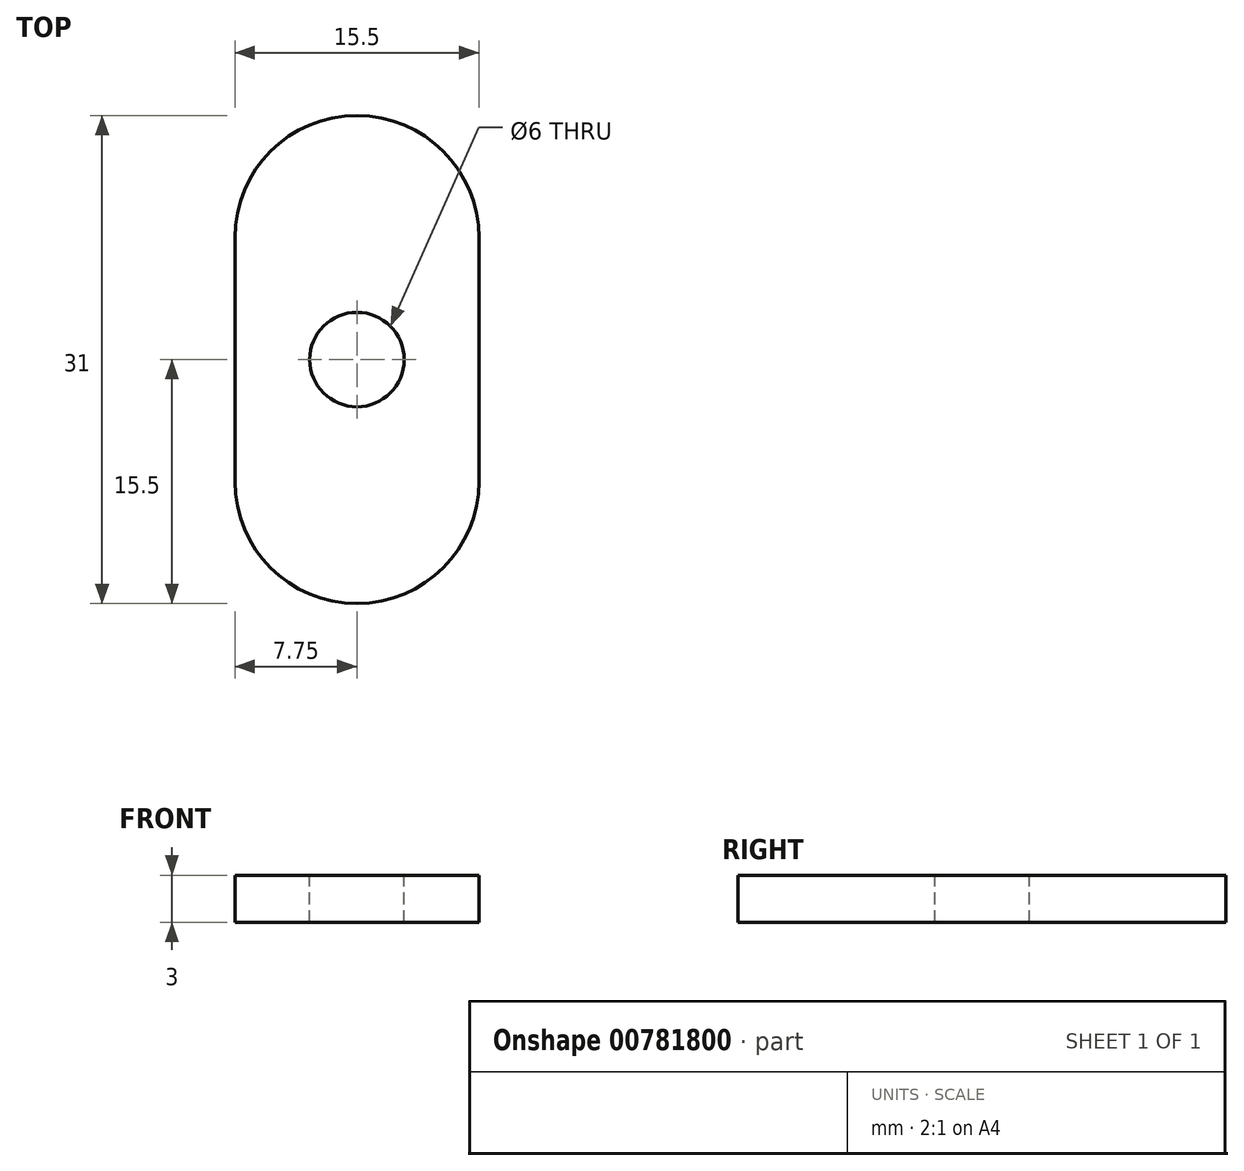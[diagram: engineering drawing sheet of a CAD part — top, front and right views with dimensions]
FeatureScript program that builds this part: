
annotation { "Feature Type Name" : "Feature", "Feature Type Description" : "" }
export const myFeature = defineFeature(function(context is Context, id is Id, definition is map)
    precondition{}
    {
        {
            var Q0;
            Q0=qCreatedBy(makeId("Top.planeOp"),FACE);
            var sketch = newSketch(context, id + "F0", { "sketchPlane" : qUnion([Q0])});
            skPoint(sketch, "E0.middle", {"position": v(0, 0) * mm});
            skPoint(sketch, "E0.top.end.orphan", {"position": v(7.75, -7.75) * mm});
            skPoint(sketch, "E0.left.end.orphan", {"position": v(-5.42, -5.42) * mm});
            skPoint(sketch, "E1.start.orphan", {"position": v(-7.75, 7.75) * mm});
            skPoint(sketch, "E0.bottom.end.orphan", {"position": v(5.42, 5.42) * mm});
            skLineSegment(sketch, "E2.left", {"start": v(-7.75, 7.75) * mm, "end": v(-7.75, -7.75) * mm});
            skLineSegment(sketch, "E2.right", {"start": v(7.75, 7.75) * mm, "end": v(7.75, -7.75) * mm});
            skArc(sketch, "E3", {"start": v(-7.75, 7.75) * mm, "mid": v(0, 15.5) * mm, "end": v(7.75, 7.75) * mm});
            skArc(sketch, "E4", {"start": v(-7.75, -7.75) * mm, "mid": v(0, -15.5) * mm, "end": v(7.75, -7.75) * mm});
            skSolve(sketch);
        }
        {
            var Q0;
            Q0 = qSketchRegion(id + "F0", true);
            extrude(context, id + "F1", {"entities" : qUnion([Q0]), "depth" : 3 * mm, "offsetDistance" : 25 * mm});
        }
        {
            var Q0;
            Q0=makeQuery(id+"F1.opExtrude","CAP_FACE",FACE,{"disambiguationData":[OSD([sQuery(id+"F0.wireOp",EDGE,"E2.left"),sQuery(id+"F0.wireOp",EDGE,"E2.right"),sQuery(id+"F0.wireOp",EDGE,"E3"),sQuery(id+"F0.wireOp",EDGE,"E4")])],"isStart":false});
            var sketch = newSketch(context, id + "F2", { "sketchPlane" : qUnion([Q0])});
            skCircle(sketch, "E5", {"center": v(0, 0) * mm, "radius": 3 * mm});
            skSolve(sketch);
        }
        {
            var Q0;
            Q0 = qSketchRegion(id + "F2", true);
            extrude(context, id + "F3", {"entities" : qUnion([Q0]), "operationType" : NewBodyOperationType.REMOVE, "oppositeDirection" : true, "depth" : 25 * mm, "offsetDistance" : 25 * mm});
        }
    });
